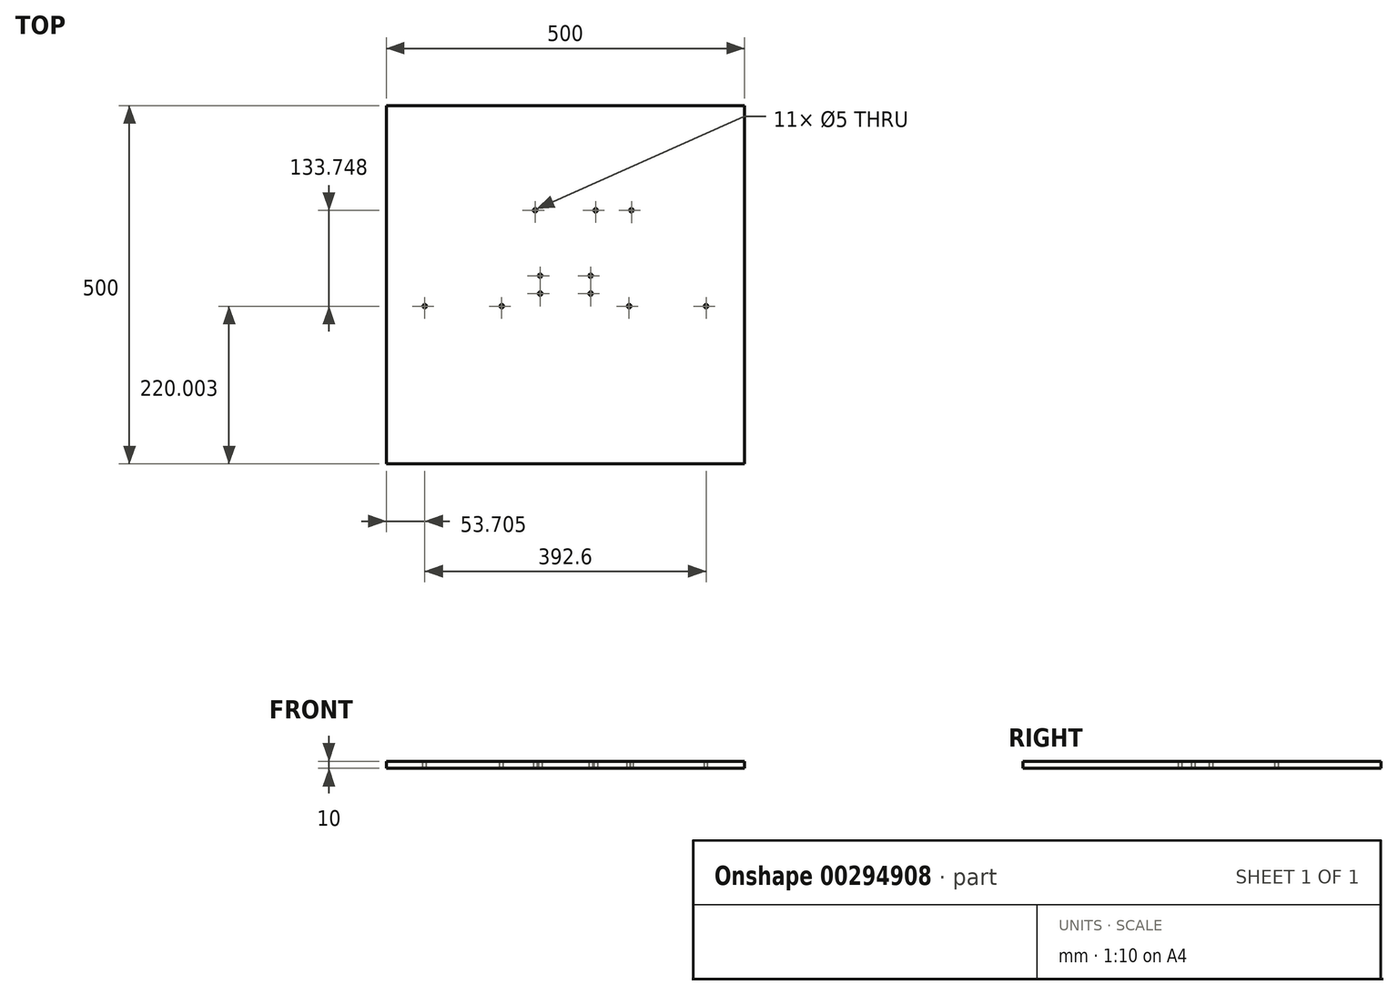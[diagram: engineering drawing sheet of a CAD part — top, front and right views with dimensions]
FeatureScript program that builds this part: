
annotation { "Feature Type Name" : "Feature", "Feature Type Description" : "" }
export const myFeature = defineFeature(function(context is Context, id is Id, definition is map)
    precondition{}
    {
        {
            var Q0;
            Q0=qCreatedBy(makeId("Top.planeOp"),FACE);
            var sketch = newSketch(context, id + "F0", { "sketchPlane" : qUnion([Q0])});
            skLineSegment(sketch, "E0.bottom", {"start": v(-257.67, 406.16) * mm, "end": v(242.33, 406.16) * mm});
            skLineSegment(sketch, "E0.top", {"start": v(-257.67, -93.84) * mm, "end": v(242.33, -93.84) * mm});
            skLineSegment(sketch, "E0.left", {"start": v(-257.67, 406.16) * mm, "end": v(-257.67, -93.84) * mm});
            skLineSegment(sketch, "E0.right", {"start": v(242.33, 406.16) * mm, "end": v(242.33, -93.84) * mm});
            skSolve(sketch);
        }
        {
            var Q0;
            Q0=makeQuery(id+"F0.imprint","IMPRINT",FACE,{"disambiguationData":[TD([[makeQuery(id+"F0.imprint","IMPRINT",EDGE,{"derivedFrom":sQuery(id+"F0.wireOp",EDGE,"E0.bottom")}),-1.0]])]});
            extrude(context, id + "F1", {"entities" : qUnion([Q0]), "depth" : 10 * mm});
        }
        {
            var Q0;
            Q0=makeQuery(id+"F1.opExtrude","CAP_FACE",FACE,{"disambiguationData":[OSD([sQuery(id+"F0.wireOp",EDGE,"E0.bottom"),sQuery(id+"F0.wireOp",EDGE,"E0.top"),sQuery(id+"F0.wireOp",EDGE,"E0.left"),sQuery(id+"F0.wireOp",EDGE,"E0.right")])],"isStart":true});
            var sketch = newSketch(context, id + "F2", { "sketchPlane" : qUnion([Q0])});
            skLineSegment(sketch, "E1", {"start": v(-7.67, -406.16) * mm, "end": v(-7.67, 93.4) * mm});
            skPoint(sketch, "E1.endSnap0", {"position": v(-7.67, 93.84) * mm});
            skLineSegment(sketch, "E2", {"start": v(242.33, -156.16) * mm, "end": v(-257.67, -156.38) * mm});
            skPoint(sketch, "E2.endSnap0", {"position": v(-257.67, -156.16) * mm});
            skPoint(sketch, "E2.endSnap1", {"position": v(-7.67, -156.38) * mm});
            skLineSegment(sketch, "E3", {"start": v(-257.67, -143.66) * mm, "end": v(242.33, -143.66) * mm, "construction": true});
            skLineSegment(sketch, "E4", {"start": v(-257.67, -168.66) * mm, "end": v(242.33, -168.66) * mm, "construction": true});
            skLineSegment(sketch, "E5", {"start": v(-42.87, 93.84) * mm, "end": v(-42.87, -406.16) * mm, "construction": true});
            skLineSegment(sketch, "E6", {"start": v(27.53, 93.84) * mm, "end": v(27.53, -406.16) * mm, "construction": true});
            skPoint(sketch, "E7", {"position": v(-42.87, -143.66) * mm});
            skPoint(sketch, "E8", {"position": v(27.53, -143.66) * mm});
            skPoint(sketch, "E9", {"position": v(27.53, -168.66) * mm});
            skPoint(sketch, "E10", {"position": v(-42.87, -168.66) * mm});
            skLineSegment(sketch, "E11", {"start": v(-49.84, 93.84) * mm, "end": v(-49.84, -406.16) * mm, "construction": true});
            skLineSegment(sketch, "E12", {"start": v(-257.67, -260) * mm, "end": v(242.33, -259.78) * mm, "construction": true});
            skPoint(sketch, "E13", {"position": v(-49.84, -259.91) * mm});
            skLineSegment(sketch, "E14", {"start": v(34.5, 93.84) * mm, "end": v(34.5, -406.16) * mm, "construction": true});
            skPoint(sketch, "E15", {"position": v(34.5, -259.87) * mm});
            skPoint(sketch, "E16", {"position": v(84.5, -259.85) * mm});
            skSolve(sketch);
        }
        {
            var Q0;
            Q0=sQuery(id+"F2.wireOp",VERTEX,"E7");
            var Q1;
            Q1=sQuery(id+"F2.wireOp",VERTEX,"E8");
            var Q2;
            Q2=sQuery(id+"F2.wireOp",VERTEX,"E9");
            var Q3;
            Q3=sQuery(id+"F2.wireOp",VERTEX,"E10");
            var Q4;
            Q4=sQuery(id+"F2.wireOp",VERTEX,"E13");
            var Q5;
            Q5=sQuery(id+"F2.wireOp",VERTEX,"E15");
            var Q6;
            Q6=sQuery(id+"F2.wireOp",VERTEX,"E16");
            var Q7;
            Q7=makeQuery(id+"F1.opExtrude","SWEPT_BODY",BODY,{"disambiguationData":[OSD([sQuery(id+"F0.wireOp",EDGE,"E0.bottom"),sQuery(id+"F0.wireOp",EDGE,"E0.top"),sQuery(id+"F0.wireOp",EDGE,"E0.left"),sQuery(id+"F0.wireOp",EDGE,"E0.right")])]});
            hole(context, id + "F3", {"style" : HoleStyle.SIMPLE, "endStyle" : HoleEndStyle.THROUGH, "holeDiameter" : 5 * mm, "tappedDepth" : 12 * mm, "tapClearance" : 3, "locations" : qUnion([Q0, Q1, Q2, Q3, Q4, Q5, Q6]), "scope" : qUnion([Q7])});
        }
        {
            var Q0;
            Q0=makeQuery(id+"F1.opExtrude","CAP_FACE",FACE,{"disambiguationData":[OSD([sQuery(id+"F0.wireOp",EDGE,"E0.bottom"),sQuery(id+"F0.wireOp",EDGE,"E0.top"),sQuery(id+"F0.wireOp",EDGE,"E0.left"),sQuery(id+"F0.wireOp",EDGE,"E0.right")])],"isStart":false});
            var sketch = newSketch(context, id + "F4", { "sketchPlane" : qUnion([Q0])});
            skLineSegment(sketch, "E17", {"start": v(-42.87, 143.66) * mm, "end": v(-257.67, 143.66) * mm, "construction": true});
            skLineSegment(sketch, "E18", {"start": v(27.53, 143.66) * mm, "end": v(242.33, 143.66) * mm, "construction": true});
            skLineSegment(sketch, "E19", {"start": v(-42.87, 168.66) * mm, "end": v(-42.87, -93.84) * mm, "construction": true});
            skLineSegment(sketch, "E20", {"start": v(27.53, 168.66) * mm, "end": v(27.53, -93.84) * mm, "construction": true});
            skLineSegment(sketch, "E21", {"start": v(-42.87, 126.16) * mm, "end": v(-257.67, 126.16) * mm, "construction": true});
            skLineSegment(sketch, "E22", {"start": v(27.53, 126.16) * mm, "end": v(242.33, 126.16) * mm, "construction": true});
            skPoint(sketch, "E23", {"position": v(-203.97, 126.16) * mm});
            skPoint(sketch, "E24", {"position": v(-96.57, 126.16) * mm});
            skPoint(sketch, "E25", {"position": v(81.23, 126.16) * mm});
            skPoint(sketch, "E26", {"position": v(188.63, 126.16) * mm});
            skSolve(sketch);
        }
        {
            var Q0;
            Q0=sQuery(id+"F4.wireOp",VERTEX,"E23");
            var Q1;
            Q1=sQuery(id+"F4.wireOp",VERTEX,"E24");
            var Q2;
            Q2=sQuery(id+"F4.wireOp",VERTEX,"E25");
            var Q3;
            Q3=sQuery(id+"F4.wireOp",VERTEX,"E26");
            var Q4;
            Q4=makeQuery(id+"F1.opExtrude","SWEPT_BODY",BODY,{"disambiguationData":[OSD([sQuery(id+"F0.wireOp",EDGE,"E0.bottom"),sQuery(id+"F0.wireOp",EDGE,"E0.top"),sQuery(id+"F0.wireOp",EDGE,"E0.left"),sQuery(id+"F0.wireOp",EDGE,"E0.right")])]});
            hole(context, id + "F5", {"style" : HoleStyle.SIMPLE, "endStyle" : HoleEndStyle.THROUGH, "holeDiameter" : 5 * mm, "tappedDepth" : 12 * mm, "tapClearance" : 3, "locations" : qUnion([Q0, Q1, Q2, Q3]), "scope" : qUnion([Q4])});
        }
    });
